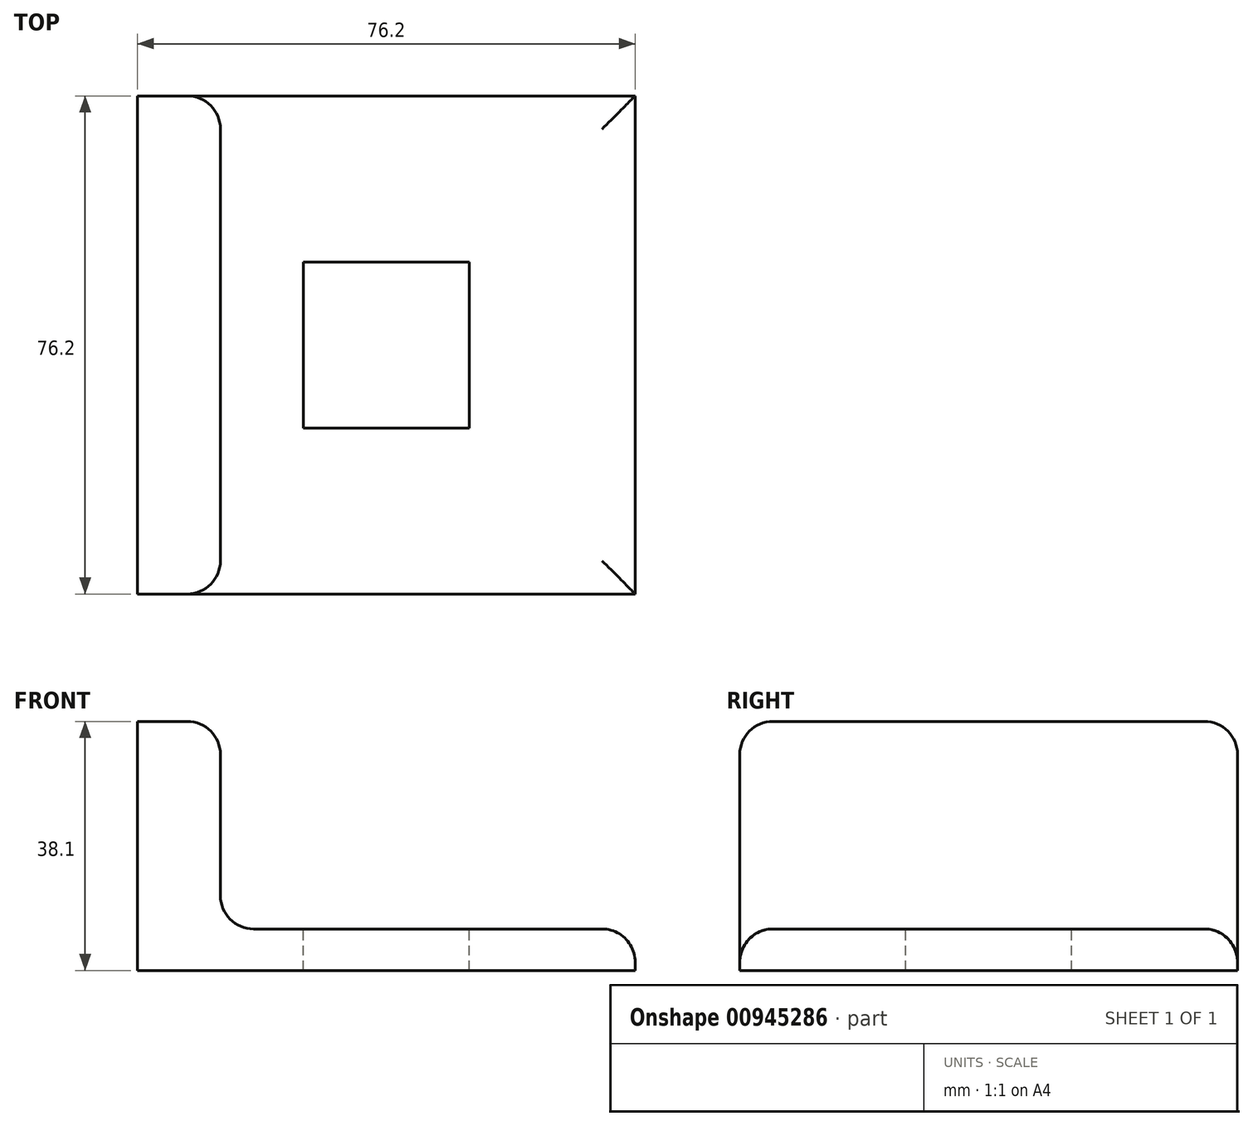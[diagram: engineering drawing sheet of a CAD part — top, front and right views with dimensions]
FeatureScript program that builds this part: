
annotation { "Feature Type Name" : "Feature", "Feature Type Description" : "" }
export const myFeature = defineFeature(function(context is Context, id is Id, definition is map)
    precondition{}
    {
        {
            var Q0;
            Q0=qCreatedBy(makeId("Top.planeOp"),FACE);
            var sketch = newSketch(context, id + "F0", { "sketchPlane" : qUnion([Q0])});
            skLineSegment(sketch, "E0.bottom", {"start": v(38.1, -38.1) * mm, "end": v(-38.1, -38.1) * mm});
            skLineSegment(sketch, "E0.top", {"start": v(38.1, 38.1) * mm, "end": v(-38.1, 38.1) * mm});
            skLineSegment(sketch, "E0.left", {"start": v(38.1, -38.1) * mm, "end": v(38.1, 38.1) * mm});
            skLineSegment(sketch, "E0.right", {"start": v(-38.1, -38.1) * mm, "end": v(-38.1, 38.1) * mm});
            skPoint(sketch, "E0.middle", {"position": v(0, 0) * mm});
            skSolve(sketch);
        }
        {
            var Q0;
            Q0=makeQuery(id+"F0.imprint","IMPRINT",FACE,{"disambiguationData":[TD([[makeQuery(id+"F0.imprint","IMPRINT",EDGE,{"derivedFrom":sQuery(id+"F0.wireOp",EDGE,"E0.bottom")}),-1.0]])]});
            extrude(context, id + "F1", {"entities" : qUnion([Q0]), "depth" : 6.35 * mm, "offsetDistance" : 25.4 * mm});
        }
        {
            var Q0;
            Q0=makeQuery(id+"F1.opExtrude","CAP_FACE",FACE,{"disambiguationData":[OSD([sQuery(id+"F0.wireOp",EDGE,"E0.bottom"),sQuery(id+"F0.wireOp",EDGE,"E0.top"),sQuery(id+"F0.wireOp",EDGE,"E0.left"),sQuery(id+"F0.wireOp",EDGE,"E0.right")])],"isStart":false});
            var sketch = newSketch(context, id + "F2", { "sketchPlane" : qUnion([Q0])});
            skLineSegment(sketch, "E1.bottom", {"start": v(12.7, -12.7) * mm, "end": v(-12.7, -12.7) * mm});
            skLineSegment(sketch, "E1.top", {"start": v(12.7, 12.7) * mm, "end": v(-12.7, 12.7) * mm});
            skLineSegment(sketch, "E1.left", {"start": v(12.7, -12.7) * mm, "end": v(12.7, 12.7) * mm});
            skLineSegment(sketch, "E1.right", {"start": v(-12.7, -12.7) * mm, "end": v(-12.7, 12.7) * mm});
            skPoint(sketch, "E1.middle", {"position": v(0, 0) * mm});
            skSolve(sketch);
        }
        {
            var Q0;
            Q0=makeQuery(id+"F2.imprint","IMPRINT",FACE,{"disambiguationData":[TD([[makeQuery(id+"F2.imprint","IMPRINT",EDGE,{"derivedFrom":sQuery(id+"F2.wireOp",EDGE,"E1.bottom")}),-1.0]])]});
            extrude(context, id + "F3", {"entities" : qUnion([Q0]), "operationType" : NewBodyOperationType.REMOVE, "oppositeDirection" : true, "depth" : 25.4 * mm, "offsetDistance" : 25.4 * mm});
        }
        {
            var Q0;
            Q0=makeQuery(id+"F1.opExtrude","CAP_FACE",FACE,{"disambiguationData":[OSD([sQuery(id+"F0.wireOp",EDGE,"E0.bottom"),sQuery(id+"F0.wireOp",EDGE,"E0.top"),sQuery(id+"F0.wireOp",EDGE,"E0.left"),sQuery(id+"F0.wireOp",EDGE,"E0.right")])],"isStart":false});
            var sketch = newSketch(context, id + "F4", { "sketchPlane" : qUnion([Q0])});
            skLineSegment(sketch, "E2.bottom", {"start": v(-38.1, 38.1) * mm, "end": v(-25.4, 38.1) * mm});
            skLineSegment(sketch, "E2.top", {"start": v(-38.1, -38.1) * mm, "end": v(-25.4, -38.1) * mm});
            skLineSegment(sketch, "E2.left", {"start": v(-38.1, 38.1) * mm, "end": v(-38.1, -38.1) * mm});
            skLineSegment(sketch, "E2.right", {"start": v(-25.4, 38.1) * mm, "end": v(-25.4, -38.1) * mm});
            skSolve(sketch);
        }
        {
            var Q0;
            Q0=makeQuery(id+"F4.imprint","IMPRINT",FACE,{"disambiguationData":[TD([[makeQuery(id+"F4.imprint","IMPRINT",EDGE,{"derivedFrom":sQuery(id+"F4.wireOp",EDGE,"E2.bottom")}),1.0]])]});
            extrude(context, id + "F5", {"entities" : qUnion([Q0]), "operationType" : NewBodyOperationType.ADD, "depth" : 31.75 * mm, "offsetDistance" : 25.4 * mm});
        }
        {
            var Q0;
            Q0=makeQuery(id+"F5.opExtrude","CAP_EDGE",EDGE,{"disambiguationData":[OSD([sQuery(id+"F4.wireOp",EDGE,"E2.right")])],"isStart":false});
            var Q1;
            Q1=makeQuery(id+"F5.opExtrude","CAP_EDGE",EDGE,{"disambiguationData":[OSD([sQuery(id+"F4.wireOp",EDGE,"E2.right")])],"isStart":true});
            fillet(context, id + "F6", {"entities" : qUnion([Q0, Q1]), "radius" : 5.08 * mm, "tangentPropagation" : true, "allowEdgeOverflow" : false});
        }
        {
            var Q0;
            Q0=makeQuery(id+"F1.opExtrude","CAP_EDGE",EDGE,{"disambiguationData":[OSD([sQuery(id+"F0.wireOp",EDGE,"E0.bottom")])],"isStart":false});
            var Q1;
            Q1=makeQuery(id+"F1.opExtrude","CAP_EDGE",EDGE,{"disambiguationData":[OSD([sQuery(id+"F0.wireOp",EDGE,"E0.left")])],"isStart":false});
            var Q2;
            Q2=makeQuery(id+"F1.opExtrude","CAP_EDGE",EDGE,{"disambiguationData":[OSD([sQuery(id+"F0.wireOp",EDGE,"E0.top")])],"isStart":false});
            fillet(context, id + "F7", {"entities" : qUnion([Q0, Q1, Q2]), "radius" : 5.08 * mm, "tangentPropagation" : true, "allowEdgeOverflow" : false});
        }
    });
